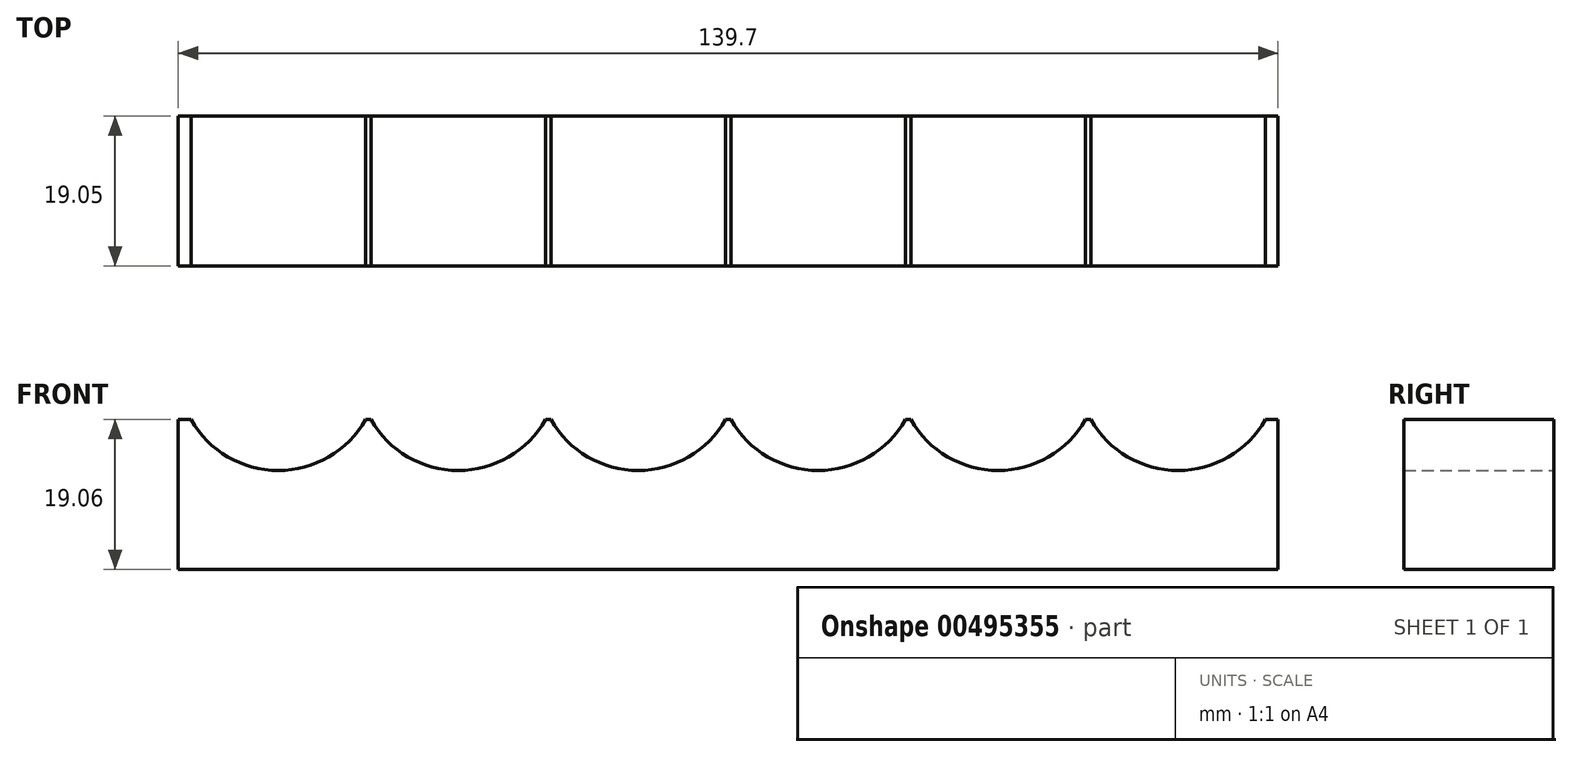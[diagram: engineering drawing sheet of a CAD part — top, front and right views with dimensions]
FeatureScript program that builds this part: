
annotation { "Feature Type Name" : "Feature", "Feature Type Description" : "" }
export const myFeature = defineFeature(function(context is Context, id is Id, definition is map)
    precondition{}
    {
        {
            var Q0;
            Q0=qCreatedBy(makeId("Front.planeOp"),FACE);
            var sketch = newSketch(context, id + "F0", { "sketchPlane" : qUnion([Q0])});
            skLineSegment(sketch, "E0.bottom", {"start": v(-58.42, 9.52) * mm, "end": v(-56.8, 9.52) * mm});
            skLineSegment(sketch, "E0.top", {"start": v(-58.42, -9.53) * mm, "end": v(81.28, -9.53) * mm});
            skLineSegment(sketch, "E0.left", {"start": v(-58.42, 9.52) * mm, "end": v(-58.42, -9.53) * mm});
            skLineSegment(sketch, "E0.right", {"start": v(81.28, 9.52) * mm, "end": v(81.28, -9.53) * mm});
            skArc(sketch, "E1", {"start": v(-11.07, 9.52) * mm, "mid": v(0, 3.05) * mm, "end": v(11.07, 9.52) * mm});
            skArc(sketch, "E2.1.0.0", {"start": v(11.79, 9.52) * mm, "mid": v(22.86, 3.05) * mm, "end": v(33.93, 9.53) * mm});
            skArc(sketch, "E2.2.0.0", {"start": v(34.65, 9.53) * mm, "mid": v(45.72, 3.05) * mm, "end": v(56.8, 9.53) * mm});
            skLineSegment(sketch, "E2.direction1", {"start": v(0, 15.75) * mm, "end": v(22.86, 15.75) * mm, "construction": true});
            skLineSegment(sketch, "E3", {"start": v(0, 0) * mm, "end": v(0, -36.17) * mm, "construction": true});
            skArc(sketch, "E4.MirrorC", {"start": v(-11.79, 9.52) * mm, "mid": v(-22.86, 3.05) * mm, "end": v(-33.93, 9.52) * mm});
            skArc(sketch, "E5.MirrorC", {"start": v(-34.65, 9.52) * mm, "mid": v(-45.72, 3.05) * mm, "end": v(-56.8, 9.52) * mm});
            skLineSegment(sketch, "E6.trimOffspring", {"start": v(56.8, 9.52) * mm, "end": v(57.5, 9.52) * mm});
            skLineSegment(sketch, "E7.trimOffspring", {"start": v(33.93, 9.52) * mm, "end": v(34.65, 9.52) * mm});
            skLineSegment(sketch, "E8.trimOffspring", {"start": v(11.07, 9.52) * mm, "end": v(11.79, 9.52) * mm});
            skLineSegment(sketch, "E9.trimOffspring", {"start": v(-11.79, 9.52) * mm, "end": v(-11.07, 9.52) * mm});
            skLineSegment(sketch, "E10.trimOffspring", {"start": v(-34.65, 9.52) * mm, "end": v(-33.93, 9.52) * mm});
            skArc(sketch, "E11.0.3.0", {"start": v(57.5, 9.52) * mm, "mid": v(68.58, 3.05) * mm, "end": v(79.65, 9.52) * mm});
            skLineSegment(sketch, "E12.trimOffspring", {"start": v(79.65, 9.52) * mm, "end": v(81.28, 9.52) * mm});
            skSolve(sketch);
        }
        {
            var Q0;
            Q0=makeQuery(id+"F0.imprint","IMPRINT",FACE,{"disambiguationData":[TD([[makeQuery(id+"F0.imprint","IMPRINT",EDGE,{"derivedFrom":sQuery(id+"F0.wireOp",EDGE,"E0.bottom")}),-1.0]])]});
            extrude(context, id + "F1", {"entities" : qUnion([Q0]), "depth" : 19.05 * mm});
        }
    });
